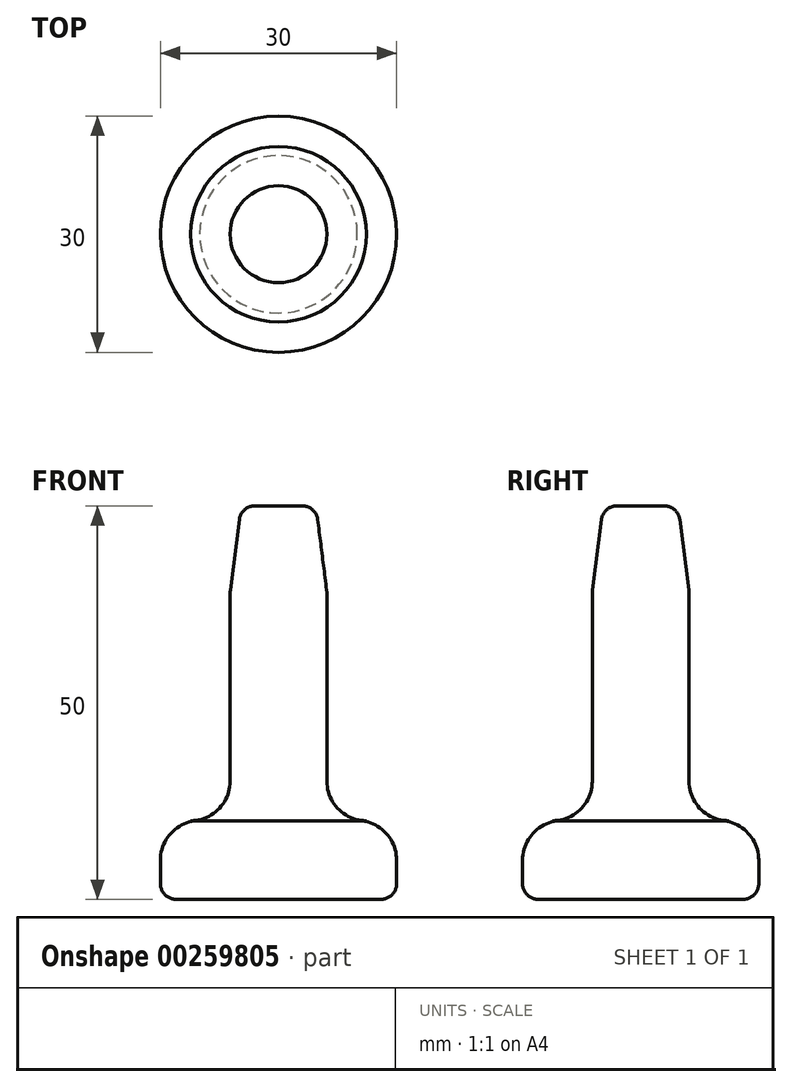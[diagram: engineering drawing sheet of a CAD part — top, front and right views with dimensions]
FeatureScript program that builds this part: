
annotation { "Feature Type Name" : "Feature", "Feature Type Description" : "" }
export const myFeature = defineFeature(function(context is Context, id is Id, definition is map)
    precondition{}
    {
        {
            var Q0;
            Q0=qCreatedBy(makeId("Front.planeOp"),FACE);
            var sketch = newSketch(context, id + "F0", { "sketchPlane" : qUnion([Q0])});
            skLineSegment(sketch, "E0", {"start": v(0, 50) * mm, "end": v(-2.99, 50) * mm});
            skLineSegment(sketch, "E1", {"start": v(0, 0) * mm, "end": v(-13, 0) * mm});
            skLineSegment(sketch, "E2", {"start": v(-15, 2) * mm, "end": v(-15, 5) * mm});
            skLineSegment(sketch, "E3", {"start": v(-11.15, 10) * mm, "end": v(-10, 10) * mm});
            skLineSegment(sketch, "E4", {"start": v(-6.15, 15) * mm, "end": v(-6.15, 38.68) * mm});
            skLineSegment(sketch, "E5", {"start": v(0, 50) * mm, "end": v(0, 0) * mm});
            skLineSegment(sketch, "E6", {"start": v(-4.97, 48.25) * mm, "end": v(-6.1, 39.31) * mm});
            skPoint(sketch, "E7.visualSharp", {"position": v(-4.75, 50) * mm});
            skArc(sketch, "E7.filletArc", {"start": v(-2.99, 50) * mm, "mid": v(-4.31, 49.5) * mm, "end": v(-4.97, 48.25) * mm});
            skPoint(sketch, "E8.visualSharp", {"position": v(-6.15, 39) * mm});
            skArc(sketch, "E8.filletArc", {"start": v(-6.1, 39.31) * mm, "mid": v(-6.14, 39) * mm, "end": v(-6.15, 38.68) * mm});
            skPoint(sketch, "E9.visualSharp", {"position": v(-6.15, 10) * mm});
            skArc(sketch, "E9.filletArc", {"start": v(-11.15, 10) * mm, "mid": v(-7.61, 11.46) * mm, "end": v(-6.15, 15) * mm});
            skPoint(sketch, "E10.visualSharp", {"position": v(-15, 10) * mm});
            skArc(sketch, "E10.filletArc", {"start": v(-10, 10) * mm, "mid": v(-13.54, 8.54) * mm, "end": v(-15, 5) * mm});
            skPoint(sketch, "E11.visualSharp", {"position": v(-15, 0) * mm});
            skArc(sketch, "E11.filletArc", {"start": v(-15, 2) * mm, "mid": v(-14.41, 0.59) * mm, "end": v(-13, 0) * mm});
            skSolve(sketch);
        }
        {
            var Q0;
            Q0=makeQuery(id+"F0.imprint","IMPRINT",FACE,{"disambiguationData":[TD([[makeQuery(id+"F0.imprint","IMPRINT",EDGE,{"derivedFrom":sQuery(id+"F0.wireOp",EDGE,"E0")}),1.0]])]});
            var Q1;
            Q1=sQuery(id+"F0.wireOp",EDGE,"E5");
            revolve(context, id + "F1", {"entities" : qUnion([Q0]), "axis" : qUnion([Q1]), "revolveType" : RevolveType.FULL});
        }
    });
